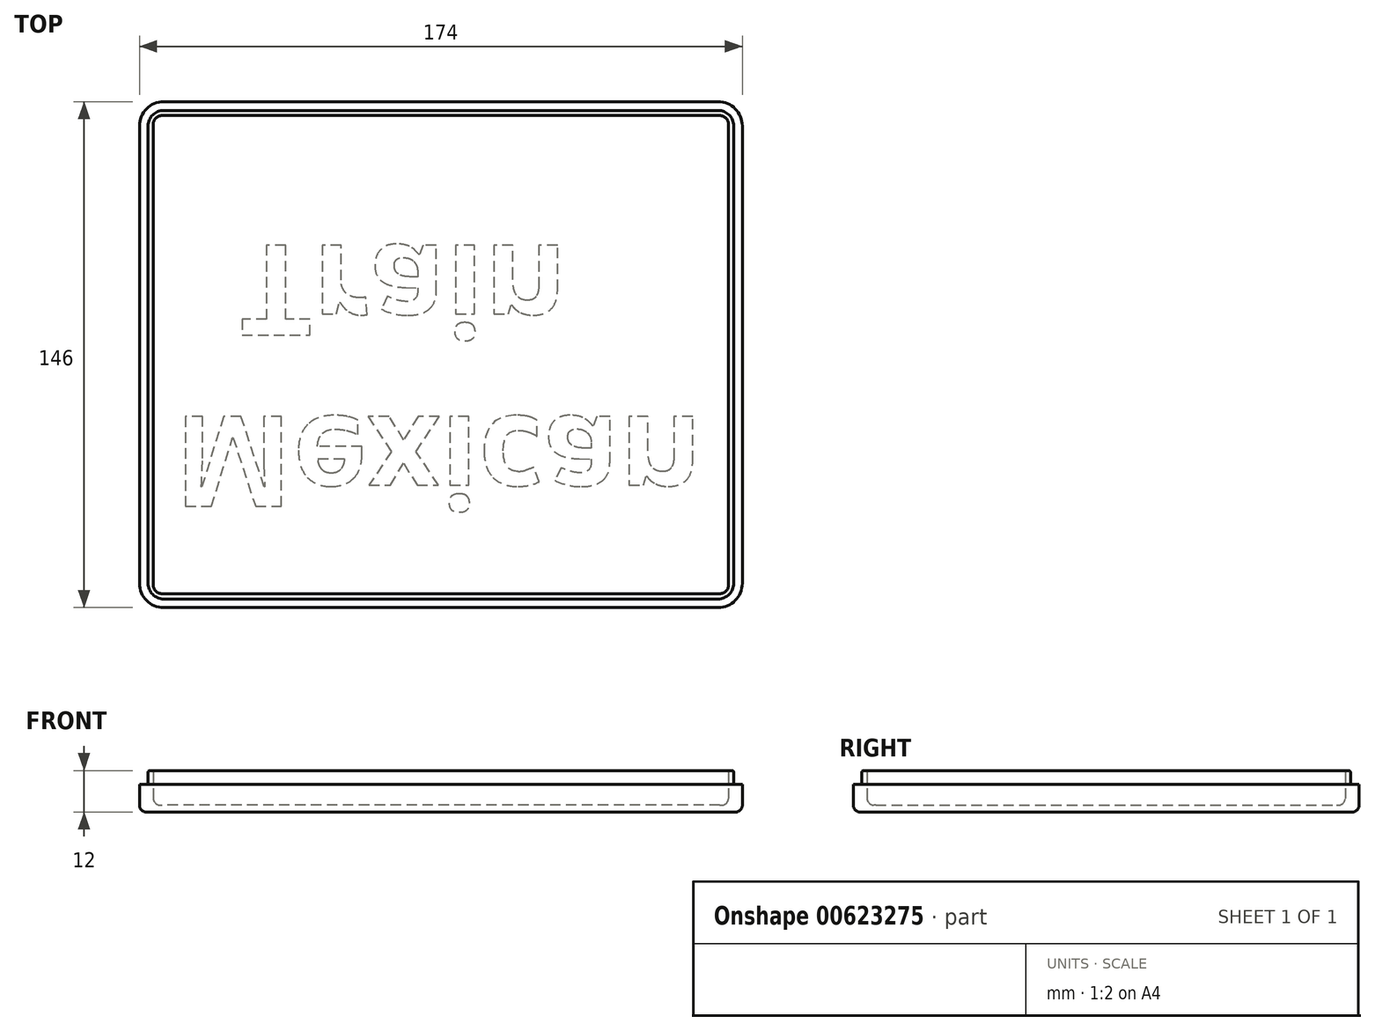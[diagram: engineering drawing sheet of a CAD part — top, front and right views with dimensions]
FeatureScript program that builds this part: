
annotation { "Feature Type Name" : "Feature", "Feature Type Description" : "" }
export const myFeature = defineFeature(function(context is Context, id is Id, definition is map)
    precondition{}
    {
        {
            var Q0;
            Q0=qCreatedBy(makeId("Top.planeOp"),FACE);
            var sketch = newSketch(context, id + "F0", { "sketchPlane" : qUnion([Q0])});
            skLineSegment(sketch, "E0.bottom", {"start": v(85, -71) * mm, "end": v(-85, -71) * mm});
            skLineSegment(sketch, "E0.top", {"start": v(85, 71) * mm, "end": v(-85, 71) * mm});
            skLineSegment(sketch, "E0.left", {"start": v(85, -71) * mm, "end": v(85, 71) * mm});
            skLineSegment(sketch, "E0.right", {"start": v(-85, -71) * mm, "end": v(-85, 71) * mm});
            skPoint(sketch, "E0.middle", {"position": v(0, 0) * mm});
            skLineSegment(sketch, "E1.bottom", {"start": v(87, -73) * mm, "end": v(-87, -73) * mm});
            skLineSegment(sketch, "E1.top", {"start": v(87, 73) * mm, "end": v(-87, 73) * mm});
            skLineSegment(sketch, "E1.left", {"start": v(87, -73) * mm, "end": v(87, 73) * mm});
            skLineSegment(sketch, "E1.right", {"start": v(-87, -73) * mm, "end": v(-87, 73) * mm});
            skSolve(sketch);
        }
        {
            var Q0;
            Q0=makeQuery(id+"F0.imprint","IMPRINT",FACE,{"disambiguationData":[TD([[makeQuery(id+"F0.imprint","IMPRINT",EDGE,{"derivedFrom":sQuery(id+"F0.wireOp",EDGE,"E0.bottom")}),-1.0]])]});
            extrude(context, id + "F1", {"entities" : qUnion([Q0]), "depth" : 2 * mm, "offsetDistance" : 25 * mm});
        }
        {
            var Q0;
            Q0=makeQuery(id+"F0.imprint","IMPRINT",FACE,{"disambiguationData":[TD([[makeQuery(id+"F0.imprint","IMPRINT",EDGE,{"derivedFrom":sQuery(id+"F0.wireOp",EDGE,"E0.bottom")}),1.0]])]});
            extrude(context, id + "F2", {"entities" : qUnion([Q0]), "operationType" : NewBodyOperationType.ADD, "depth" : 2 * mm, "offsetDistance" : 25 * mm});
        }
        {
            var Q0;
            {var subQ0=sQuery(id+"F0.wireOp",EDGE,"E0.right");var subQ1=sQuery(id+"F0.wireOp",EDGE,"E0.left");var subQ2=sQuery(id+"F0.wireOp",EDGE,"E0.top");var subQ3=sQuery(id+"F0.wireOp",EDGE,"E0.bottom");Q0=makeQuery(id+"F2.boolean.opBoolean","MERGE",FACE,{"derivedFrom":[makeQuery(id+"F1.opExtrude","CAP_FACE",FACE,{"disambiguationData":[OSD([subQ3,subQ2,subQ1,subQ0])],"isStart":false}),makeQuery(id+"F2.opExtrude","CAP_FACE",FACE,{"disambiguationData":[OSD([subQ3,subQ2,subQ1,subQ0,sQuery(id+"F0.wireOp",EDGE,"E1.bottom"),sQuery(id+"F0.wireOp",EDGE,"E1.top"),sQuery(id+"F0.wireOp",EDGE,"E1.left"),sQuery(id+"F0.wireOp",EDGE,"E1.right")])],"isStart":false})]});}
            var sketch = newSketch(context, id + "F3", { "sketchPlane" : qUnion([Q0])});
            skLineSegment(sketch, "E2.bottom", {"start": v(84.5, -70.5) * mm, "end": v(-84.5, -70.5) * mm});
            skLineSegment(sketch, "E2.top", {"start": v(84.5, 70.5) * mm, "end": v(-84.5, 70.5) * mm});
            skLineSegment(sketch, "E2.left", {"start": v(84.5, -70.5) * mm, "end": v(84.5, 70.5) * mm});
            skLineSegment(sketch, "E2.right", {"start": v(-84.5, -70.5) * mm, "end": v(-84.5, 70.5) * mm});
            skPoint(sketch, "E2.middle", {"position": v(0, 0) * mm});
            skLineSegment(sketch, "E3.bottom", {"start": v(83, -69) * mm, "end": v(-83, -69) * mm});
            skLineSegment(sketch, "E3.top", {"start": v(83, 69) * mm, "end": v(-83, 69) * mm});
            skLineSegment(sketch, "E3.left", {"start": v(83, -69) * mm, "end": v(83, 69) * mm});
            skLineSegment(sketch, "E3.right", {"start": v(-83, -69) * mm, "end": v(-83, 69) * mm});
            skSolve(sketch);
        }
        {
            var Q0;
            Q0=makeQuery(id+"F3.imprint","IMPRINT",FACE,{"disambiguationData":[TD([[makeQuery(id+"F3.imprint","IMPRINT",EDGE,{"derivedFrom":sQuery(id+"F3.wireOp",EDGE,"E2.bottom")}),-1.0]])]});
            extrude(context, id + "F4", {"entities" : qUnion([Q0]), "operationType" : NewBodyOperationType.ADD, "depth" : 10 * mm, "offsetDistance" : 25 * mm});
        }
        {
            var Q0;
            Q0=makeQuery(id+"F4.opExtrude","SWEPT_EDGE",EDGE,{"disambiguationData":[OSD([sQuery(id+"F3.wireOp",EDGE,"E3.bottom"),sQuery(id+"F3.wireOp",EDGE,"E3.right")])]});
            var Q1;
            Q1=makeQuery(id+"F4.opExtrude","SWEPT_EDGE",EDGE,{"disambiguationData":[OSD([sQuery(id+"F3.wireOp",EDGE,"E3.top"),sQuery(id+"F3.wireOp",EDGE,"E3.right")])]});
            var Q2;
            Q2=makeQuery(id+"F4.opExtrude","SWEPT_EDGE",EDGE,{"disambiguationData":[OSD([sQuery(id+"F3.wireOp",EDGE,"E3.top"),sQuery(id+"F3.wireOp",EDGE,"E3.left")])]});
            var Q3;
            Q3=makeQuery(id+"F4.opExtrude","SWEPT_EDGE",EDGE,{"disambiguationData":[OSD([sQuery(id+"F3.wireOp",EDGE,"E3.bottom"),sQuery(id+"F3.wireOp",EDGE,"E3.left")])]});
            fillet(context, id + "F5", {"entities" : qUnion([Q0, Q1, Q2, Q3]), "radius" : 2.5 * mm, "tangentPropagation" : true, "allowEdgeOverflow" : false});
        }
        {
            var Q0;
            Q0=makeQuery(id+"F4.opExtrude","SWEPT_EDGE",EDGE,{"disambiguationData":[OSD([sQuery(id+"F3.wireOp",EDGE,"E2.top"),sQuery(id+"F3.wireOp",EDGE,"E2.right")])]});
            var Q1;
            Q1=makeQuery(id+"F4.opExtrude","SWEPT_EDGE",EDGE,{"disambiguationData":[OSD([sQuery(id+"F3.wireOp",EDGE,"E2.bottom"),sQuery(id+"F3.wireOp",EDGE,"E2.right")])]});
            var Q2;
            Q2=makeQuery(id+"F4.opExtrude","SWEPT_EDGE",EDGE,{"disambiguationData":[OSD([sQuery(id+"F3.wireOp",EDGE,"E2.bottom"),sQuery(id+"F3.wireOp",EDGE,"E2.left")])]});
            var Q3;
            Q3=makeQuery(id+"F4.opExtrude","SWEPT_EDGE",EDGE,{"disambiguationData":[OSD([sQuery(id+"F3.wireOp",EDGE,"E2.top"),sQuery(id+"F3.wireOp",EDGE,"E2.left")])]});
            fillet(context, id + "F6", {"entities" : qUnion([Q0, Q1, Q2, Q3]), "radius" : 4.5 * mm, "tangentPropagation" : true, "allowEdgeOverflow" : false});
        }
        {
            var Q0;
            Q0=makeQuery(id+"F2.opExtrude","SWEPT_EDGE",EDGE,{"disambiguationData":[OSD([sQuery(id+"F0.wireOp",EDGE,"E1.bottom"),sQuery(id+"F0.wireOp",EDGE,"E1.right")])]});
            var Q1;
            Q1=makeQuery(id+"F2.opExtrude","SWEPT_EDGE",EDGE,{"disambiguationData":[OSD([sQuery(id+"F0.wireOp",EDGE,"E1.bottom"),sQuery(id+"F0.wireOp",EDGE,"E1.left")])]});
            var Q2;
            Q2=makeQuery(id+"F2.opExtrude","SWEPT_EDGE",EDGE,{"disambiguationData":[OSD([sQuery(id+"F0.wireOp",EDGE,"E1.top"),sQuery(id+"F0.wireOp",EDGE,"E1.left")])]});
            var Q3;
            Q3=makeQuery(id+"F2.opExtrude","SWEPT_EDGE",EDGE,{"disambiguationData":[OSD([sQuery(id+"F0.wireOp",EDGE,"E1.top"),sQuery(id+"F0.wireOp",EDGE,"E1.right")])]});
            fillet(context, id + "F7", {"entities" : qUnion([Q0, Q1, Q2, Q3]), "radius" : 7 * mm, "tangentPropagation" : true, "allowEdgeOverflow" : false});
        }
        {
            var Q0;
            {var subQ0=sQuery(id+"F0.wireOp",EDGE,"E0.right");var subQ1=sQuery(id+"F0.wireOp",EDGE,"E0.left");var subQ2=sQuery(id+"F0.wireOp",EDGE,"E0.top");var subQ3=sQuery(id+"F0.wireOp",EDGE,"E0.bottom");Q0=makeQuery(id+"F2.boolean.opBoolean","MERGE",FACE,{"derivedFrom":[makeQuery(id+"F1.opExtrude","CAP_FACE",FACE,{"disambiguationData":[OSD([subQ3,subQ2,subQ1,subQ0])],"isStart":true}),makeQuery(id+"F2.opExtrude","CAP_FACE",FACE,{"disambiguationData":[OSD([subQ3,subQ2,subQ1,subQ0,sQuery(id+"F0.wireOp",EDGE,"E1.bottom"),sQuery(id+"F0.wireOp",EDGE,"E1.top"),sQuery(id+"F0.wireOp",EDGE,"E1.left"),sQuery(id+"F0.wireOp",EDGE,"E1.right")])],"isStart":true})]});}
            var sketch = newSketch(context, id + "F8", { "sketchPlane" : qUnion([Q0])});
            skLineSegment(sketch, "E4", {"start": v(-77, 73) * mm, "end": v(-77, -73) * mm, "construction": true});
            skLineSegment(sketch, "E5", {"start": v(-87, 48) * mm, "end": v(87, 48) * mm, "construction": true});
            skText(sketch, "E6", { "text": "Mexican\n  Train", "fontName": "OpenSans-Bold.ttf"});
            skLineSegment(sketch, "E7", {"start": v(-87, 56.62) * mm, "end": v(-77, 56.62) * mm, "construction": true});
            skLineSegment(sketch, "E8", {"start": v(-68.03, 73) * mm, "end": v(-68.03, 48) * mm, "construction": true});
            const initialGuessF8  = {"E6": [-0.077, 0.01783, 1, 0, 0.02617]};
            skSetInitialGuess(sketch, initialGuessF8);
            skSolve(sketch);
        }
        {
            var Q0;
            Q0=makeQuery(id+"F8.imprint","IMPRINT",FACE,{"disambiguationData":[TD([[makeQuery(id+"F8.imprint","IMPRINT",EDGE,{"derivedFrom":sQuery(id+"F8.wireOp",EDGE,"E6.sketch_text.stroke-0")}),-1.0]])]});
            var Q1;
            Q1=makeQuery(id+"F8.imprint","IMPRINT",FACE,{"disambiguationData":[TD([[makeQuery(id+"F8.imprint","IMPRINT",EDGE,{"derivedFrom":sQuery(id+"F8.wireOp",EDGE,"E6.sketch_text.stroke-19")}),-1.0]])]});
            var Q2;
            Q2=makeQuery(id+"F8.imprint","IMPRINT",FACE,{"disambiguationData":[TD([[makeQuery(id+"F8.imprint","IMPRINT",EDGE,{"derivedFrom":sQuery(id+"F8.wireOp",EDGE,"E6.sketch_text.stroke-39")}),-1.0]])]});
            var Q3;
            Q3=makeQuery(id+"F8.imprint","IMPRINT",FACE,{"disambiguationData":[TD([[makeQuery(id+"F8.imprint","IMPRINT",EDGE,{"derivedFrom":sQuery(id+"F8.wireOp",EDGE,"E6.sketch_text.stroke-56")}),-1.0]])]});
            var Q4;
            Q4=makeQuery(id+"F8.imprint","IMPRINT",FACE,{"disambiguationData":[TD([[makeQuery(id+"F8.imprint","IMPRINT",EDGE,{"derivedFrom":sQuery(id+"F8.wireOp",EDGE,"E6.sketch_text.stroke-51")}),-1.0]])]});
            var Q5;
            Q5=makeQuery(id+"F8.imprint","IMPRINT",FACE,{"disambiguationData":[TD([[makeQuery(id+"F8.imprint","IMPRINT",EDGE,{"derivedFrom":sQuery(id+"F8.wireOp",EDGE,"E6.sketch_text.stroke-60")}),-1.0]])]});
            var Q6;
            Q6=makeQuery(id+"F8.imprint","IMPRINT",FACE,{"disambiguationData":[TD([[makeQuery(id+"F8.imprint","IMPRINT",EDGE,{"derivedFrom":sQuery(id+"F8.wireOp",EDGE,"E6.sketch_text.stroke-74")}),-1.0]])]});
            var Q7;
            Q7=makeQuery(id+"F8.imprint","IMPRINT",FACE,{"disambiguationData":[TD([[makeQuery(id+"F8.imprint","IMPRINT",EDGE,{"derivedFrom":sQuery(id+"F8.wireOp",EDGE,"E6.sketch_text.stroke-99")}),-1.0]])]});
            var Q8;
            Q8=makeQuery(id+"F8.imprint","IMPRINT",FACE,{"disambiguationData":[TD([[makeQuery(id+"F8.imprint","IMPRINT",EDGE,{"derivedFrom":sQuery(id+"F8.wireOp",EDGE,"E6.sketch_text.stroke-116")}),-1.0]])]});
            var Q9;
            Q9=makeQuery(id+"F8.imprint","IMPRINT",FACE,{"disambiguationData":[TD([[makeQuery(id+"F8.imprint","IMPRINT",EDGE,{"derivedFrom":sQuery(id+"F8.wireOp",EDGE,"E6.sketch_text.stroke-124")}),-1.0]])]});
            var Q10;
            Q10=makeQuery(id+"F8.imprint","IMPRINT",FACE,{"disambiguationData":[TD([[makeQuery(id+"F8.imprint","IMPRINT",EDGE,{"derivedFrom":sQuery(id+"F8.wireOp",EDGE,"E6.sketch_text.stroke-137")}),-1.0]])]});
            var Q11;
            Q11=makeQuery(id+"F8.imprint","IMPRINT",FACE,{"disambiguationData":[TD([[makeQuery(id+"F8.imprint","IMPRINT",EDGE,{"derivedFrom":sQuery(id+"F8.wireOp",EDGE,"E6.sketch_text.stroke-167")}),-1.0]])]});
            var Q12;
            Q12=makeQuery(id+"F8.imprint","IMPRINT",FACE,{"disambiguationData":[TD([[makeQuery(id+"F8.imprint","IMPRINT",EDGE,{"derivedFrom":sQuery(id+"F8.wireOp",EDGE,"E6.sketch_text.stroke-162")}),-1.0]])]});
            var Q13;
            Q13=makeQuery(id+"F8.imprint","IMPRINT",FACE,{"disambiguationData":[TD([[makeQuery(id+"F8.imprint","IMPRINT",EDGE,{"derivedFrom":sQuery(id+"F8.wireOp",EDGE,"E6.sketch_text.stroke-171")}),-1.0]])]});
            extrude(context, id + "F9", {"entities" : qUnion([Q0, Q1, Q2, Q3, Q4, Q5, Q6, Q7, Q8, Q9, Q10, Q11, Q12, Q13]), "operationType" : NewBodyOperationType.REMOVE, "oppositeDirection" : true, "depth" : .1 * mm, "offsetDistance" : 25 * mm});
        }
        {
            var Q0;
            Q0=makeQuery(id+"F4.opExtrude","CAP_FACE",FACE,{"disambiguationData":[OSD([sQuery(id+"F3.wireOp",EDGE,"E2.bottom"),sQuery(id+"F3.wireOp",EDGE,"E2.top"),sQuery(id+"F3.wireOp",EDGE,"E2.left"),sQuery(id+"F3.wireOp",EDGE,"E2.right"),sQuery(id+"F3.wireOp",EDGE,"E3.bottom"),sQuery(id+"F3.wireOp",EDGE,"E3.top"),sQuery(id+"F3.wireOp",EDGE,"E3.left"),sQuery(id+"F3.wireOp",EDGE,"E3.right")])],"isStart":false});
            fillet(context, id + "F10", {"entities" : qUnion([Q0]), "radius" : .5 * mm, "tangentPropagation" : true, "allowEdgeOverflow" : false});
        }
        {
            var Q0;
            Q0=makeQuery(id+"F2.opExtrude","CAP_EDGE",EDGE,{"disambiguationData":[OSD([sQuery(id+"F0.wireOp",EDGE,"E1.bottom")])],"isStart":true});
            fillet(context, id + "F11", {"entities" : qUnion([Q0]), "radius" : 2 * mm, "tangentPropagation" : true, "allowEdgeOverflow" : false});
        }
        {
            var Q0;
            {var subQ0=sQuery(id+"F0.wireOp",EDGE,"E0.right");var subQ1=sQuery(id+"F0.wireOp",EDGE,"E0.left");var subQ2=sQuery(id+"F0.wireOp",EDGE,"E0.top");var subQ3=sQuery(id+"F0.wireOp",EDGE,"E0.bottom");Q0=makeQuery(id+"F4.boolean.opBoolean","SPLIT",FACE,{"disambiguationData":[TD([makeQuery(id+"F4.opExtrude","SWEPT_FACE",FACE,{"disambiguationData":[OSD([sQuery(id+"F3.wireOp",EDGE,"E3.bottom")])]})])],"derivedFrom":makeQuery(id+"F2.boolean.opBoolean","MERGE",FACE,{"derivedFrom":[makeQuery(id+"F1.opExtrude","CAP_FACE",FACE,{"disambiguationData":[OSD([subQ3,subQ2,subQ1,subQ0])],"isStart":false}),makeQuery(id+"F2.opExtrude","CAP_FACE",FACE,{"disambiguationData":[OSD([subQ3,subQ2,subQ1,subQ0,sQuery(id+"F0.wireOp",EDGE,"E1.bottom"),sQuery(id+"F0.wireOp",EDGE,"E1.top"),sQuery(id+"F0.wireOp",EDGE,"E1.left"),sQuery(id+"F0.wireOp",EDGE,"E1.right")])],"isStart":false})]})});}
            fillet(context, id + "F12", {"entities" : qUnion([Q0]), "radius" : 2 * mm, "tangentPropagation" : true, "allowEdgeOverflow" : false});
        }
        {
            var Q0;
            {var subQ0=sQuery(id+"F0.wireOp",EDGE,"E1.right");var subQ1=sQuery(id+"F0.wireOp",EDGE,"E1.left");var subQ2=sQuery(id+"F0.wireOp",EDGE,"E1.top");var subQ3=sQuery(id+"F0.wireOp",EDGE,"E1.bottom");var subQ4=sQuery(id+"F0.wireOp",EDGE,"E0.right");var subQ5=sQuery(id+"F0.wireOp",EDGE,"E0.left");var subQ6=sQuery(id+"F0.wireOp",EDGE,"E0.top");var subQ7=sQuery(id+"F0.wireOp",EDGE,"E0.bottom");Q0=makeQuery(id+"F4.boolean.opBoolean","SPLIT",FACE,{"disambiguationData":[TD([makeQuery(id+"F2.opExtrude","SWEPT_FACE",FACE,{"disambiguationData":[OSD([subQ3])]})])],"derivedFrom":makeQuery(id+"F2.boolean.opBoolean","MERGE",FACE,{"derivedFrom":[makeQuery(id+"F1.opExtrude","CAP_FACE",FACE,{"disambiguationData":[OSD([subQ7,subQ6,subQ5,subQ4])],"isStart":false}),makeQuery(id+"F2.opExtrude","CAP_FACE",FACE,{"disambiguationData":[OSD([subQ7,subQ6,subQ5,subQ4,subQ3,subQ2,subQ1,subQ0])],"isStart":false})]})});}
            extrude(context, id + "F13", {"entities" : qUnion([Q0]), "operationType" : NewBodyOperationType.ADD, "depth" : 6 * mm, "offsetDistance" : 25 * mm});
        }
    });
